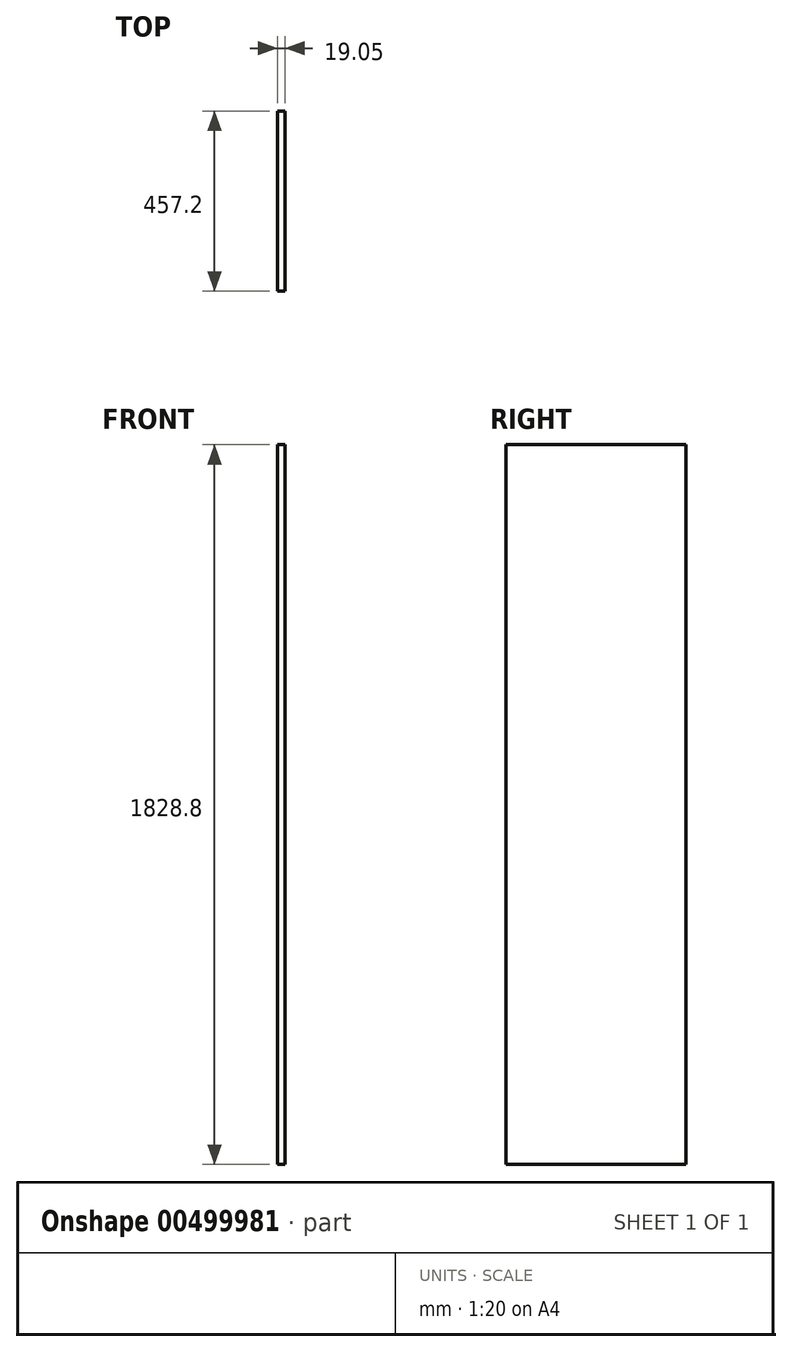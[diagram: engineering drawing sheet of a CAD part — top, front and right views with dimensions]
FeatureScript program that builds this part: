
annotation { "Feature Type Name" : "Feature", "Feature Type Description" : "" }
export const myFeature = defineFeature(function(context is Context, id is Id, definition is map)
    precondition{}
    {
        {
            var Q0;
            Q0=qCreatedBy(makeId("Right.planeOp"),FACE);
            var sketch = newSketch(context, id + "F0", { "sketchPlane" : qUnion([Q0])});
            skLineSegment(sketch, "E0.bottom", {"start": v(-228.6, 914.4) * mm, "end": v(228.6, 914.4) * mm});
            skLineSegment(sketch, "E0.top", {"start": v(-228.6, -914.4) * mm, "end": v(228.6, -914.4) * mm});
            skLineSegment(sketch, "E0.left", {"start": v(-228.6, 914.4) * mm, "end": v(-228.6, -914.4) * mm});
            skLineSegment(sketch, "E0.right", {"start": v(228.6, 914.4) * mm, "end": v(228.6, -914.4) * mm});
            skPoint(sketch, "E0.middle", {"position": v(0, 0) * mm});
            skLineSegment(sketch, "E1.bottom", {"start": v(-228.6, -914.4) * mm, "end": v(990.6, -914.4) * mm});
            skSolve(sketch);
        }
        {
            var Q0;
            Q0=qSketchRegion(id+"F0",true);
            extrude(context, id + "F1", {"entities" : qUnion([Q0]), "depth" : 19.05 * mm, "offsetDistance" : 25.4 * mm});
        }
    });
